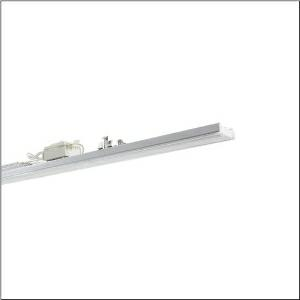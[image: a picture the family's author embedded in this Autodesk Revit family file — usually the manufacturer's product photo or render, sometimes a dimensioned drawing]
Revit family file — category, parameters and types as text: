
# Revit family: licross_21_recessed_mo_52te197n48xg
name_source: partatom
category: Lighting Fixtures
units: mm (PartAtom-declared; Revit-internal decimal feet)

## family parameters
Cut with Voids When Loaded = No
Host = Face
Light Source = No
Part Type = Normal
Room Calculation Point = No
Round Connector Dimension = Use Diameter
Shared = No

## types (1)
- Licross 21 Recessed MO (1 x LED, 8450 lm, 47.9 W, 4000K)
    Apparent Load = 48 VA
    CIE Flux Codes = 55 90 98 100 100
    Color Rendering = 80
    Color Temperature = 4000K
    Default Elevation = 1800 mm
    Description = Licross 21 Recessed MO, luminaire insert, of sheet steel, galvanised, coil coated, white, length: 1.500mm, width: 66mm, height: 67mm, LED rated luminous flux: 8.450lm, light colour: 840, SDCM (Standard Deviation of Colour Matching)MacAdam ≤ 3 SDCM (initial), control gear: ON/OFF, with plug, 3-pole, with phase selection, mains connection: 220..240V, AC, 50/60Hz, rated input power: 48W, internal wiring halogen-free, primary light control with lens, of plastic, primary optical cover: cover, of PMMA, light emission: direct distribution, primary light characteristic: double asymmetric, protection rating (complete): IP54, insulation class (complete): insulation class I (protective earthing), certification: CE, ENEC, VDE, UKCA, protection symbol: D if used in an environment with non-conductive dust loads with corresponding accessories, impact resistance: IK06, permissible ambient temperature for indoor applications: -35..+40°C, corresponds to IFS (International Featured Standards) requirements for safety and quality in the food industry, reducing of maximum allowable ambient temperature of 5°C with ceiling mounting, LABS conformity tested according to VDMA 24364:2018-05, The light source and the operating device comply with the requirements of the Ecodesign Regulation (EU) 2019/2020 and are replaceable in accordance with this regulation, packaging unit: 1 piece
    Height = 58 mm
    Lamp = 1 x LED
    Lamp Light Flux = 8450 lm
    Lamp Power = 47.9 W
    Lamp count = 1
    Length = 1500 mm
    Luminous efficacy = 176 lm/W
    Manufacturer = Siteco
    ModVariant = No
    Model = 52TE197N48XG
    Mounting Place = Ceiling
    Mounting Type = Pendant
    Number of Poles = 1
    OnlyDefault = Yes
    Power Factor = 1
    Product Name = Licross 21 Recessed MO
    Product group = luminaire insert | ceiling pendant
    ProductGroupID = 901
    Protection Class = Protection class I
    Protection Degree = IP 54
    RLX_Detail_Level = 1
    RLX_Emergency_Light_Flux = 0 lm
    RLX_Emergency_Type = 0
    RLX_Emergency_Type_DB = No
    RlxData = <blob elided: 21177 chars, md5=08d5c1f2>
    Socket = socket
    Standby Power = 0 W
    System Light Flux = 8450 lm
    System Power = 48 W
    Type Comments = Product without accessories
    Type Image = l_1296930.jpg
    URL = http://relux.com
    VarID = ---
    Voltage = 0 V
    Weight = 0.00 kg
    Width = 66 mm

## geometry (parser evidence)
native form markers: Blend x4, Sweep x10
no freeform markers — native parametric forms only
